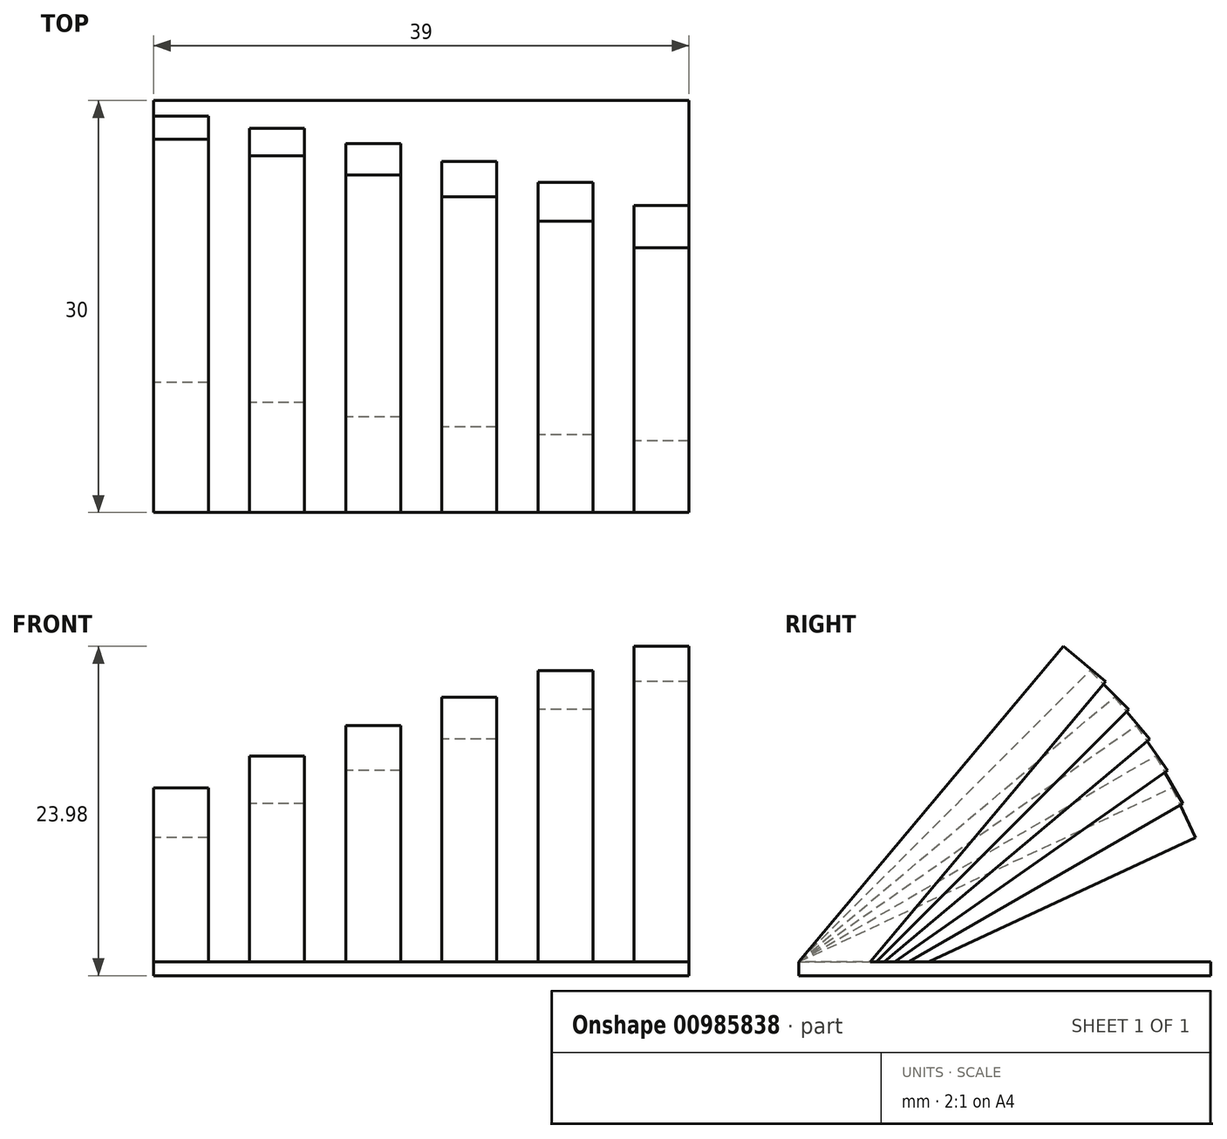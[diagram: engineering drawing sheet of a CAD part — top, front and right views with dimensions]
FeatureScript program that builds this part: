
annotation { "Feature Type Name" : "Feature", "Feature Type Description" : "" }
export const myFeature = defineFeature(function(context is Context, id is Id, definition is map)
    precondition{}
    {
        {
            assignVariable(context, id + "F0", {"name" : "angle_width", "anyValue" : 4 * mm});
        }
        {
            assignVariable(context, id + "F1", {"name" : "spacing_distance", "anyValue" : 3 * mm});
        }
        {
            var Q0;
            Q0=qCreatedBy(makeId("Top.planeOp"),FACE);
            var sketch = newSketch(context, id + "F2", { "sketchPlane" : qUnion([Q0])});
            skLineSegment(sketch, "E0.bottom", {"start": v(19.5, -15) * mm, "end": v(-19.5, -15) * mm});
            skLineSegment(sketch, "E0.top", {"start": v(19.5, 15) * mm, "end": v(-19.5, 15) * mm});
            skLineSegment(sketch, "E0.left", {"start": v(19.5, -15) * mm, "end": v(19.5, 15) * mm});
            skLineSegment(sketch, "E0.right", {"start": v(-19.5, -15) * mm, "end": v(-19.5, 15) * mm});
            skPoint(sketch, "E0.middle", {"position": v(0, 0) * mm});
            skSolve(sketch);
        }
        {
            var Q0;
            Q0=makeQuery(id+"F2.imprint","IMPRINT",FACE,{"disambiguationData":[TD([[makeQuery(id+"F2.imprint","IMPRINT",EDGE,{"derivedFrom":sQuery(id+"F2.wireOp",EDGE,"E0.bottom")}),-1.0]])]});
            extrude(context, id + "F3", {"entities" : qUnion([Q0]), "depth" : 1 * mm, "offsetDistance" : 25 * mm});
        }
        {
            var Q0;
            Q0=makeQuery(id+"F3.opExtrude","SWEPT_FACE",FACE,{"disambiguationData":[OSD([sQuery(id+"F2.wireOp",EDGE,"E0.right")])]});
            var sketch = newSketch(context, id + "F4", { "sketchPlane" : qUnion([Q0])});
            skLineSegment(sketch, "E1.0", {"start": v(15, 1) * mm, "end": v(-15, 1) * mm});
            skLineSegment(sketch, "E2", {"start": v(15, 1) * mm, "end": v(-12.19, 13.68) * mm});
            skLineSegment(sketch, "E3", {"start": v(-12.19, 13.68) * mm, "end": v(-13.88, 10.05) * mm});
            skLineSegment(sketch, "E4", {"start": v(-13.88, 10.05) * mm, "end": v(5.54, 1) * mm});
            skSolve(sketch);
        }
        {
            var Q0;
            {var subQ0=sQuery(id+"F4.wireOp",EDGE,"E2");Q0=makeQuery(id+"F4.imprint","IMPRINT",FACE,{"disambiguationData":[TD([[makeQuery(id+"F4.imprint","IMPRINT",EDGE,{"derivedFrom":subQ0}),1.0]])]});}
            extrude(context, id + "F5", {"entities" : qUnion([Q0]), "operationType" : NewBodyOperationType.ADD, "oppositeDirection" : true, "depth" : getVariable(context, 'angle_width'), "offsetDistance" : 25 * mm});
        }
        {
            var Q0;
            Q0=makeQuery(id+"F5.opExtrude","CAP_FACE",FACE,{"disambiguationData":[OSD([sQuery(id+"F4.wireOp",EDGE,"E1.0"),sQuery(id+"F4.wireOp",EDGE,"E2"),sQuery(id+"F4.wireOp",EDGE,"E3"),sQuery(id+"F4.wireOp",EDGE,"E4")])],"isStart":false});
            cPlane(context, id + "F6", {"entities" : qUnion([Q0]), "cplaneType" : CPlaneType.OFFSET, "offset" : getVariable(context, 'spacing_distance'), "width" : 150 * mm, "height" : 150 * mm});
        }
        {
            var Q0;
            Q0=qCreatedBy(id+"F6.planeOp",FACE);
            var sketch = newSketch(context, id + "F7", { "sketchPlane" : qUnion([Q0])});
            skLineSegment(sketch, "E5.0.1", {"start": v(-5.54, 1) * mm, "end": v(-15, 1) * mm});
            skLineSegment(sketch, "E5.0.3", {"start": v(-15, 1) * mm, "end": v(15, 1) * mm});
            skLineSegment(sketch, "E5.0.5", {"start": v(15, 1) * mm, "end": v(-5.54, 1) * mm});
            skLineSegment(sketch, "E6", {"start": v(-15, 1) * mm, "end": v(10.98, 16) * mm});
            skLineSegment(sketch, "E7", {"start": v(10.98, 16) * mm, "end": v(12.98, 12.54) * mm});
            skLineSegment(sketch, "E8", {"start": v(12.98, 12.54) * mm, "end": v(-7, 1) * mm});
            skSolve(sketch);
        }
        {
            var Q0;
            {var subQ0=sQuery(id+"F7.wireOp",EDGE,"E6");Q0=makeQuery(id+"F7.imprint","IMPRINT",FACE,{"disambiguationData":[TD([[makeQuery(id+"F7.imprint","IMPRINT",EDGE,{"derivedFrom":subQ0}),-1.0]])]});}
            extrude(context, id + "F8", {"entities" : qUnion([Q0]), "operationType" : NewBodyOperationType.ADD, "depth" : getVariable(context, 'angle_width'), "offsetDistance" : 25 * mm});
        }
        {
            var Q0;
            Q0=makeQuery(id+"F8.opExtrude","CAP_FACE",FACE,{"disambiguationData":[OSD([sQuery(id+"F7.wireOp",EDGE,"E5.0.3"),sQuery(id+"F7.wireOp",EDGE,"E6"),sQuery(id+"F7.wireOp",EDGE,"E7"),sQuery(id+"F7.wireOp",EDGE,"E8")])],"isStart":false});
            cPlane(context, id + "F9", {"entities" : qUnion([Q0]), "cplaneType" : CPlaneType.OFFSET, "offset" : getVariable(context, 'spacing_distance'), "width" : 150 * mm, "height" : 150 * mm});
        }
        {
            var Q0;
            Q0=qCreatedBy(id+"F9.planeOp",FACE);
            var sketch = newSketch(context, id + "F10", { "sketchPlane" : qUnion([Q0])});
            skLineSegment(sketch, "E9.0.1", {"start": v(-15, 1) * mm, "end": v(-7, 1) * mm});
            skLineSegment(sketch, "E9.0.3", {"start": v(-7, 1) * mm, "end": v(-15, 1) * mm});
            skLineSegment(sketch, "E9.0.5", {"start": v(-15, 1) * mm, "end": v(15, 1) * mm});
            skLineSegment(sketch, "E9.0.7", {"start": v(15, 1) * mm, "end": v(-5.54, 1) * mm});
            skLineSegment(sketch, "E9.0.9", {"start": v(-5.54, 1) * mm, "end": v(-15, 1) * mm});
            skLineSegment(sketch, "E10", {"start": v(-15, 1) * mm, "end": v(9.57, 18.2) * mm});
            skLineSegment(sketch, "E11", {"start": v(9.57, 18.2) * mm, "end": v(11.87, 14.93) * mm});
            skLineSegment(sketch, "E12", {"start": v(11.87, 14.93) * mm, "end": v(-8.03, 1) * mm});
            skSolve(sketch);
        }
        {
            var Q0;
            {var subQ0=sQuery(id+"F10.wireOp",EDGE,"E10");Q0=makeQuery(id+"F10.imprint","IMPRINT",FACE,{"disambiguationData":[TD([[makeQuery(id+"F10.imprint","IMPRINT",EDGE,{"derivedFrom":subQ0}),-1.0]])]});}
            extrude(context, id + "F11", {"entities" : qUnion([Q0]), "operationType" : NewBodyOperationType.ADD, "depth" : getVariable(context, 'angle_width'), "offsetDistance" : 25 * mm});
        }
        {
            var Q0;
            Q0=makeQuery(id+"F11.opExtrude","CAP_FACE",FACE,{"disambiguationData":[OSD([sQuery(id+"F10.wireOp",EDGE,"E9.0.9"),sQuery(id+"F10.wireOp",EDGE,"E10"),sQuery(id+"F10.wireOp",EDGE,"E11"),sQuery(id+"F10.wireOp",EDGE,"E12")])],"isStart":false});
            cPlane(context, id + "F12", {"entities" : qUnion([Q0]), "cplaneType" : CPlaneType.OFFSET, "offset" : getVariable(context, 'spacing_distance'), "width" : 150 * mm, "height" : 150 * mm});
        }
        {
            var Q0;
            Q0=qCreatedBy(id+"F12.planeOp",FACE);
            var sketch = newSketch(context, id + "F13", { "sketchPlane" : qUnion([Q0])});
            skLineSegment(sketch, "E13.0.0", {"start": v(-15, 1) * mm, "end": v(-8.03, 1) * mm});
            skLineSegment(sketch, "E13.0.2", {"start": v(-8.03, 1) * mm, "end": v(-15, 1) * mm});
            skLineSegment(sketch, "E13.0.4", {"start": v(-15, 1) * mm, "end": v(15, 1) * mm});
            skLineSegment(sketch, "E13.0.6", {"start": v(15, 1) * mm, "end": v(-5.54, 1) * mm});
            skLineSegment(sketch, "E13.0.8", {"start": v(-5.54, 1) * mm, "end": v(-15, 1) * mm});
            skLineSegment(sketch, "E13.0.10", {"start": v(-15, 1) * mm, "end": v(-7, 1) * mm});
            skLineSegment(sketch, "E13.0.12", {"start": v(-7, 1) * mm, "end": v(-15, 1) * mm});
            skLineSegment(sketch, "E14", {"start": v(-15, 1) * mm, "end": v(7.98, 20.28) * mm});
            skLineSegment(sketch, "E15", {"start": v(7.98, 20.28) * mm, "end": v(10.55, 17.22) * mm});
            skLineSegment(sketch, "E16", {"start": v(10.55, 17.22) * mm, "end": v(-8.78, 1) * mm});
            skSolve(sketch);
        }
        {
            var Q0;
            {var subQ0=sQuery(id+"F13.wireOp",EDGE,"E14");Q0=makeQuery(id+"F13.imprint","IMPRINT",FACE,{"disambiguationData":[TD([[makeQuery(id+"F13.imprint","IMPRINT",EDGE,{"derivedFrom":subQ0}),-1.0]])]});}
            extrude(context, id + "F14", {"entities" : qUnion([Q0]), "operationType" : NewBodyOperationType.ADD, "depth" : getVariable(context, 'angle_width'), "offsetDistance" : 25 * mm});
        }
        {
            var Q0;
            Q0=makeQuery(id+"F14.opExtrude","CAP_FACE",FACE,{"disambiguationData":[OSD([sQuery(id+"F13.wireOp",EDGE,"E13.0.12"),sQuery(id+"F13.wireOp",EDGE,"E14"),sQuery(id+"F13.wireOp",EDGE,"E15"),sQuery(id+"F13.wireOp",EDGE,"E16")])],"isStart":false});
            cPlane(context, id + "F15", {"entities" : qUnion([Q0]), "cplaneType" : CPlaneType.OFFSET, "offset" : getVariable(context, 'spacing_distance'), "width" : 150 * mm, "height" : 150 * mm});
        }
        {
            var Q0;
            Q0=qCreatedBy(id+"F15.planeOp",FACE);
            var sketch = newSketch(context, id + "F16", { "sketchPlane" : qUnion([Q0])});
            skLineSegment(sketch, "E17.0.0", {"start": v(-15, 1) * mm, "end": v(-8.78, 1) * mm});
            skLineSegment(sketch, "E17.0.2", {"start": v(-8.78, 1) * mm, "end": v(-15, 1) * mm});
            skLineSegment(sketch, "E17.0.4", {"start": v(-15, 1) * mm, "end": v(15, 1) * mm});
            skLineSegment(sketch, "E17.0.6", {"start": v(15, 1) * mm, "end": v(-5.54, 1) * mm});
            skLineSegment(sketch, "E17.0.8", {"start": v(-5.54, 1) * mm, "end": v(-15, 1) * mm});
            skLineSegment(sketch, "E17.0.10", {"start": v(-15, 1) * mm, "end": v(-7, 1) * mm});
            skLineSegment(sketch, "E17.0.12", {"start": v(-7, 1) * mm, "end": v(-15, 1) * mm});
            skLineSegment(sketch, "E17.0.14", {"start": v(-15, 1) * mm, "end": v(-8.03, 1) * mm});
            skLineSegment(sketch, "E17.0.16", {"start": v(-8.03, 1) * mm, "end": v(-15, 1) * mm});
            skLineSegment(sketch, "E18", {"start": v(-15, 1) * mm, "end": v(6.21, 22.21) * mm});
            skLineSegment(sketch, "E19", {"start": v(6.21, 22.21) * mm, "end": v(9.04, 19.38) * mm});
            skLineSegment(sketch, "E20", {"start": v(9.04, 19.38) * mm, "end": v(-9.34, 1) * mm});
            skSolve(sketch);
        }
        {
            var Q0;
            {var subQ0=sQuery(id+"F16.wireOp",EDGE,"E18");Q0=makeQuery(id+"F16.imprint","IMPRINT",FACE,{"disambiguationData":[TD([[makeQuery(id+"F16.imprint","IMPRINT",EDGE,{"derivedFrom":subQ0}),-1.0]])]});}
            extrude(context, id + "F17", {"entities" : qUnion([Q0]), "operationType" : NewBodyOperationType.ADD, "depth" : getVariable(context, 'angle_width'), "offsetDistance" : 25 * mm});
        }
        {
            var Q0;
            Q0=makeQuery(id+"F17.opExtrude","CAP_FACE",FACE,{"disambiguationData":[OSD([sQuery(id+"F16.wireOp",EDGE,"E17.0.16"),sQuery(id+"F16.wireOp",EDGE,"E18"),sQuery(id+"F16.wireOp",EDGE,"E19"),sQuery(id+"F16.wireOp",EDGE,"E20")])],"isStart":false});
            cPlane(context, id + "F18", {"entities" : qUnion([Q0]), "cplaneType" : CPlaneType.OFFSET, "offset" : getVariable(context, 'spacing_distance'), "width" : 150 * mm, "height" : 150 * mm});
        }
        {
            var Q0;
            Q0=qCreatedBy(id+"F18.planeOp",FACE);
            var sketch = newSketch(context, id + "F19", { "sketchPlane" : qUnion([Q0])});
            skLineSegment(sketch, "E21.0.0", {"start": v(-15, 1) * mm, "end": v(-9.34, 1) * mm});
            skLineSegment(sketch, "E21.0.2", {"start": v(-9.34, 1) * mm, "end": v(-15, 1) * mm});
            skLineSegment(sketch, "E21.0.4", {"start": v(-15, 1) * mm, "end": v(15, 1) * mm});
            skLineSegment(sketch, "E21.0.6", {"start": v(15, 1) * mm, "end": v(-5.54, 1) * mm});
            skLineSegment(sketch, "E21.0.8", {"start": v(-5.54, 1) * mm, "end": v(-15, 1) * mm});
            skLineSegment(sketch, "E21.0.10", {"start": v(-15, 1) * mm, "end": v(-7, 1) * mm});
            skLineSegment(sketch, "E21.0.12", {"start": v(-7, 1) * mm, "end": v(-15, 1) * mm});
            skLineSegment(sketch, "E21.0.14", {"start": v(-15, 1) * mm, "end": v(-8.03, 1) * mm});
            skLineSegment(sketch, "E21.0.16", {"start": v(-8.03, 1) * mm, "end": v(-15, 1) * mm});
            skLineSegment(sketch, "E21.0.18", {"start": v(-15, 1) * mm, "end": v(-8.78, 1) * mm});
            skLineSegment(sketch, "E21.0.20", {"start": v(-8.78, 1) * mm, "end": v(-15, 1) * mm});
            skLineSegment(sketch, "E22", {"start": v(-15, 1) * mm, "end": v(4.28, 23.98) * mm});
            skLineSegment(sketch, "E23", {"start": v(4.28, 23.98) * mm, "end": v(7.35, 21.41) * mm});
            skLineSegment(sketch, "E24", {"start": v(7.35, 21.41) * mm, "end": v(-9.78, 1) * mm});
            skSolve(sketch);
        }
        {
            var Q0;
            {var subQ0=sQuery(id+"F19.wireOp",EDGE,"E22");Q0=makeQuery(id+"F19.imprint","IMPRINT",FACE,{"disambiguationData":[TD([[makeQuery(id+"F19.imprint","IMPRINT",EDGE,{"derivedFrom":subQ0}),-1.0]])]});}
            extrude(context, id + "F20", {"entities" : qUnion([Q0]), "operationType" : NewBodyOperationType.ADD, "depth" : getVariable(context, 'angle_width'), "offsetDistance" : 25 * mm});
        }
    });
